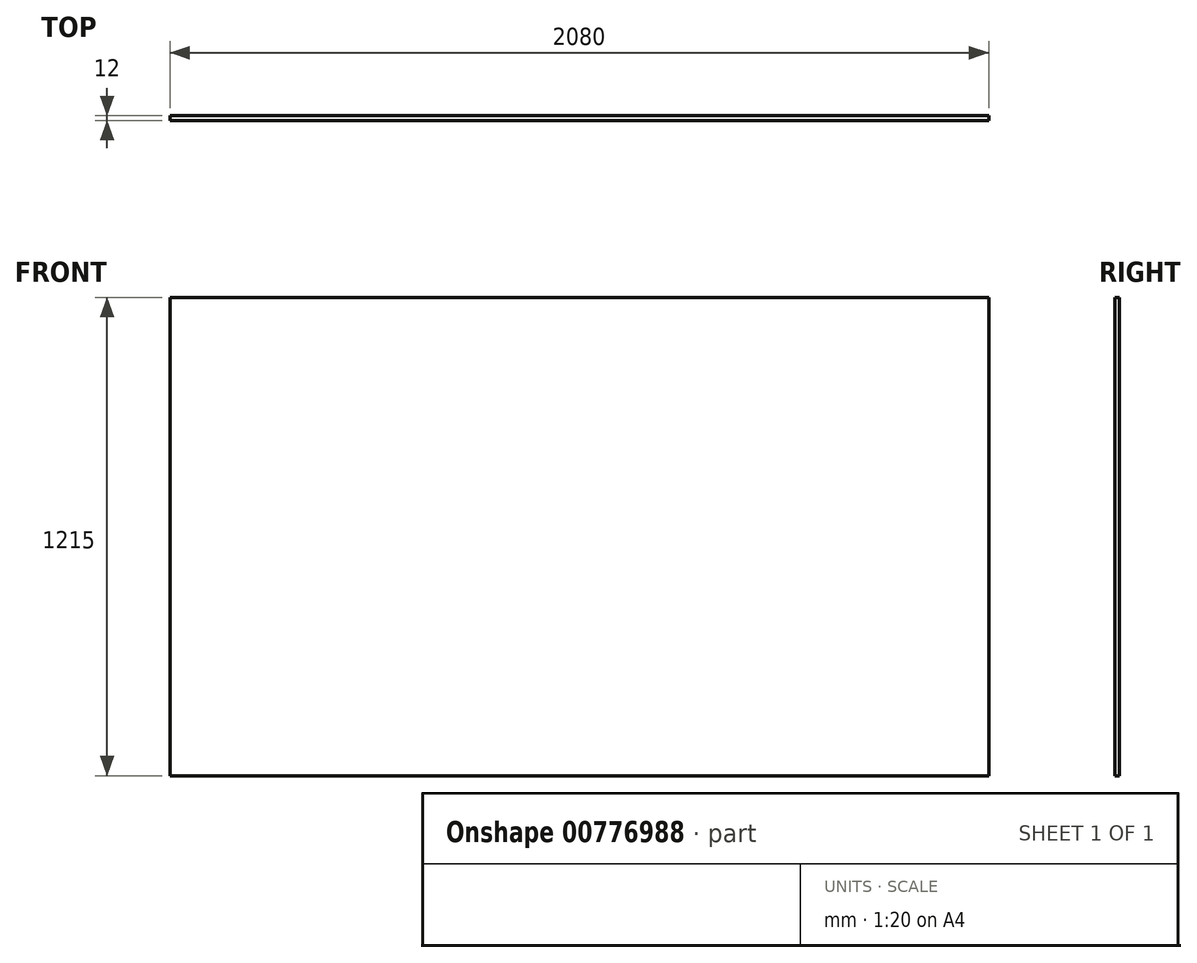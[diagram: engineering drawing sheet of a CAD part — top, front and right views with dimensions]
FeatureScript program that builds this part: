
annotation { "Feature Type Name" : "Feature", "Feature Type Description" : "" }
export const myFeature = defineFeature(function(context is Context, id is Id, definition is map)
    precondition{}
    {
        {
            var Q0;
            Q0=qCreatedBy(makeId("Front.planeOp"),FACE);
            var sketch = newSketch(context, id + "F0", { "sketchPlane" : qUnion([Q0])});
            skLineSegment(sketch, "E0.bottom", {"start": v(-1071.48, 782.93) * mm, "end": v(1008.52, 782.93) * mm});
            skLineSegment(sketch, "E0.top", {"start": v(-1071.48, -432.07) * mm, "end": v(1008.52, -432.07) * mm});
            skLineSegment(sketch, "E0.left", {"start": v(-1071.48, 782.93) * mm, "end": v(-1071.48, -432.07) * mm});
            skLineSegment(sketch, "E0.right", {"start": v(1008.52, 782.93) * mm, "end": v(1008.52, -432.07) * mm});
            skSolve(sketch);
        }
        {
            var Q0;
            Q0 = qSketchRegion(id + "F0", true);
            extrude(context, id + "F1", {"entities" : qUnion([Q0]), "depth" : 12 * mm, "offsetDistance" : 25 * mm});
        }
    });
